# Revit family: Data_Device-Network-Leviton-Shutted_Adapter_Plates-OPT_X-SDX-5F100
name_source: partatom
category: Data Devices
units: mm (PartAtom-declared; Revit-internal decimal feet)

## family parameters
Cut with Voids When Loaded = No
Host = Face
Maintain Annotation Orientation = Yes
OmniClass Number = 23.85.50.17
OmniClass Title = Communication and Data Processing Equipment
Part Type = Normal
Room Calculation Point = No
Round Connector Dimension = Use Diameter
Shared = Yes

## types (10) — shared parameters
Assembly Code = D5030600
Date Last Modified = April 19, 2024
Default Elevation = 24 "
Equipment Abbreviation = SAP
Family Version = 1.0.0
Has ID Windows = No
Manufacturer = Leviton
Model Disclaimer = http://www.leviton.com
Plate Material = Steel - Leviton - Powdercoat - Black
Shielded = No
URL = http://www.leviton.com
zero-valued in all types: Minimum Order Quantity, Quantity per Package

## per-type parameters (varying)
| type | Adapter Material | Description | Part Description | z Is 12 Fibers | z Is 24 Fibers | z Leviton Type |
| 24 Fiber, OS2, Quad LC/APC Shuttered (Green) | Plastic - Leviton - Green | 24-Fiber (Black), OS2, Quad LC/APC Shuttered (Green), Zirconia Ceramic Sleeve. | 24-Fiber (Black), OS2, Quad LC/APC Shuttered (Green), Zirconia Ceramic Sleeve. | No | Yes | 10 |
| 24 Fiber, OS2, Quad LC Shuttered (Blue) | Plastic - Leviton - Blue | 24-Fiber (Black), OS2, Quad LC Shuttered (Blue), Zirconia Ceramic Sleeve. | 24-Fiber (Black), OS2, Quad LC Shuttered (Blue), Zirconia Ceramic Sleeve. | No | Yes | 9 |
| 24 Fiber, OM4, Quad LC Shuttered (Heather Violet) | Plastic - Leviton - Heather Violet | 24-Fiber (Black), OM4, Quad LC Shuttered (Heather Violet), Zirconia Ceramic Sleeve. | 24-Fiber (Black), OM4, Quad LC Shuttered (Heather Violet), Zirconia Ceramic Sleeve. | No | Yes | 8 |
| 24 Fiber, OM3 & OM4, Quad LC Shuttered (Aqua) | Plastic - Leviton - Aqua | 24-Fiber (Black), OM3 & OM4, Quad LC Shuttered (Aqua), Zirconia Ceramic Sleeve. | 24-Fiber (Black), OM3 & OM4, Quad LC Shuttered (Aqua), Zirconia Ceramic Sleeve. | No | Yes | 7 |
| 12 Fiber, OS2, Duplex LC/APC Shuttered (Green) | Plastic - Leviton - Green | 12-Fiber (Black), OS2, Duplex LC/APC Shuttered (Green), Zirconia Ceramic Sleeve. | 12-Fiber (Black), OS2, Duplex LC/APC Shuttered (Green), Zirconia Ceramic Sleeve. | Yes | No | 5 |
| 12 Fiber, OS2, Duplex LC Shuttered (Blue) | Plastic - Leviton - Blue | 12-Fiber (Black), OS2, Duplex LC Shuttered (Blue), Zirconia Ceramic Sleeve. | 12-Fiber (Black), OS2, Duplex LC Shuttered (Blue), Zirconia Ceramic Sleeve. | Yes | No | 4 |
| 12 Fiber, OM4, Duplex LC Shuttered (Heather Violet) | Plastic - Leviton - Heather Violet | 12-Fiber (Black), OM4, Duplex LC Shuttered (Heather Violet), Zirconia Ceramic Sleeve. | 12-Fiber (Black), OM4, Duplex LC Shuttered (Heather Violet), Zirconia Ceramic Sleeve. | Yes | No | 3 |
| 12 Fiber, OM3 & OM4, Duplex LC Shuttered (Aqua) | Plastic - Leviton - Aqua | 12-Fiber (Black), OM3 & OM4, Duplex LC Shuttered (Aqua), Zirconia Ceramic Sleeve. | 12-Fiber (Black), OM3 & OM4, Duplex LC Shuttered (Aqua), Zirconia Ceramic Sleeve. | Yes | No | 2 |
| 24 Fiber, OM1, Quad LC Shuttered (Beige) | Plastic - Leviton - Beige | 24-Fiber (Black), OM1, Quad LC Shuttered (Beige), Zirconia Ceramic Sleeve. | 24-Fiber (Black), OM1, Quad LC Shuttered (Beige), Zirconia Ceramic Sleeve. | No | Yes | 6 |
| 12 Fiber, OM1, Duplex LC Shuttered (Beige) | Plastic - Leviton - Beige | 12-Fiber (Black), OM1, Duplex LC Shuttered (Beige), Zirconia Ceramic Sleeve. | 12-Fiber (Black), OM1, Duplex LC Shuttered (Beige), Zirconia Ceramic Sleeve. | Yes | No | 1 |

## geometry (parser evidence)
native form markers: Blend x12, Sweep x7
no freeform markers — native parametric forms only
